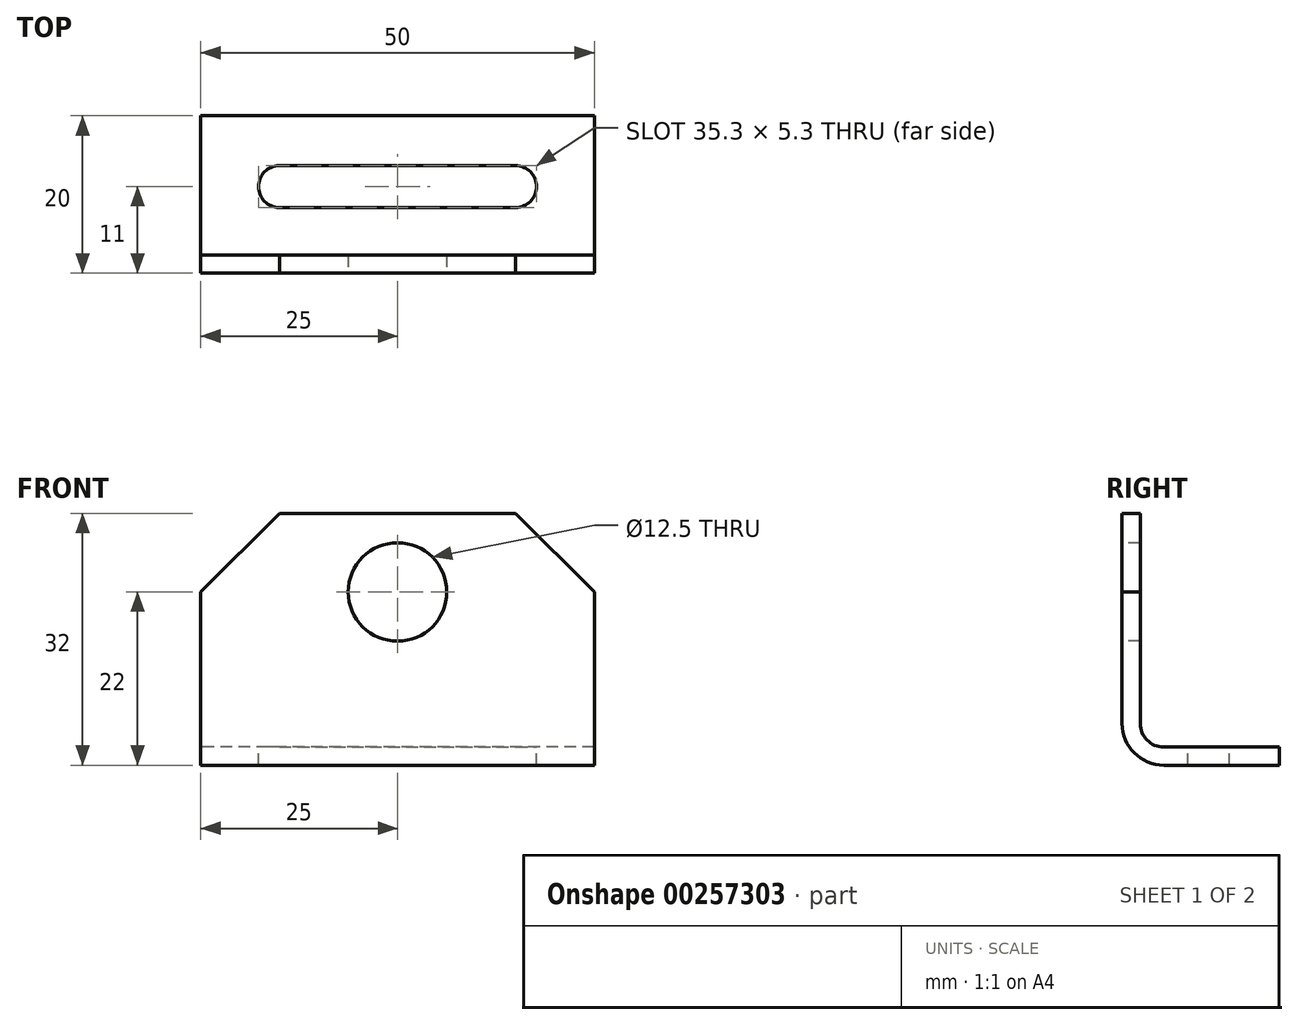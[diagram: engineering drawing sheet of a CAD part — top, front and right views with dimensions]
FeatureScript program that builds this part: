
annotation { "Feature Type Name" : "Feature", "Feature Type Description" : "" }
export const myFeature = defineFeature(function(context is Context, id is Id, definition is map)
    precondition{}
    {
        {
            var Q0;
            Q0=qCreatedBy(makeId("Right.planeOp"),FACE);
            var sketch = newSketch(context, id + "F0", { "sketchPlane" : qUnion([Q0])});
            skLineSegment(sketch, "E0", {"start": v(0, 32) * mm, "end": v(0, 0) * mm});
            skLineSegment(sketch, "E1", {"start": v(0, 0) * mm, "end": v(20, 0) * mm});
            skLineSegment(sketch, "E2", {"start": v(20, 0) * mm, "end": v(20, 2.3) * mm});
            skLineSegment(sketch, "E3", {"start": v(20, 2.3) * mm, "end": v(2.3, 2.3) * mm});
            skLineSegment(sketch, "E4", {"start": v(2.3, 2.3) * mm, "end": v(2.3, 32) * mm});
            skLineSegment(sketch, "E5", {"start": v(2.3, 32) * mm, "end": v(0, 32) * mm});
            skSolve(sketch);
        }
        {
            var Q0;
            Q0 = qSketchRegion(id + "F0", true);
            extrude(context, id + "F1", {"entities" : qUnion([Q0]), "depth" : 25 * mm, "hasSecondDirection" : true, "secondDirectionOppositeDirection" : true, "secondDirectionDepth" : 25 * mm});
        }
        {
            var Q0;
            Q0=makeQuery(id+"F1.opExtrude","SWEPT_FACE",FACE,{"disambiguationData":[OSD([sQuery(id+"F0.wireOp",EDGE,"E0")])]});
            var sketch = newSketch(context, id + "F2", { "sketchPlane" : qUnion([Q0])});
            skPoint(sketch, "E6", {"position": v(0, 22) * mm});
            skSolve(sketch);
        }
        {
            var Q0;
            Q0=makeQuery(id+"F1.opExtrude","SWEPT_FACE",FACE,{"disambiguationData":[OSD([sQuery(id+"F0.wireOp",EDGE,"E3")])]});
            var sketch = newSketch(context, id + "F3", { "sketchPlane" : qUnion([Q0])});
            skLineSegment(sketch, "E7", {"start": v(-20.02, 11) * mm, "end": v(21.78, 11) * mm, "construction": true});
            skLineSegment(sketch, "E8", {"start": v(15, 16.43) * mm, "end": v(15, 4.1) * mm, "construction": true});
            skArc(sketch, "E9", {"start": v(15, 8.35) * mm, "mid": v(17.65, 11) * mm, "end": v(15, 13.65) * mm});
            skLineSegment(sketch, "E10.0", {"start": v(-15.06, 8.35) * mm, "end": v(15, 8.35) * mm});
            skLineSegment(sketch, "E11.MirrorCS", {"start": v(-15.06, 13.65) * mm, "end": v(15, 13.65) * mm});
            skArc(sketch, "E12.MirrorC", {"start": v(-15, 8.35) * mm, "mid": v(-17.65, 11) * mm, "end": v(-15, 13.65) * mm});
            skPoint(sketch, "E13", {"position": v(-17.65, 11) * mm});
            skSolve(sketch);
        }
        {
            var Q0;
            {var subQ0=sQuery(id+"F3.wireOp",EDGE,"E9");Q0=makeQuery(id+"F3.imprint","IMPRINT",FACE,{"disambiguationData":[TD([[makeQuery(id+"F3.imprint","IMPRINT",EDGE,{"derivedFrom":subQ0}),1.0]])]});}
            extrude(context, id + "F4", {"entities" : qUnion([Q0]), "operationType" : NewBodyOperationType.REMOVE, "endBound" : BoundingType.THROUGH_ALL, "oppositeDirection" : true, "depth" : 25 * mm});
        }
        {
            var Q0;
            Q0=makeQuery(id+"F1.opExtrude","SWEPT_EDGE",EDGE,{"disambiguationData":[OSD([sQuery(id+"F0.wireOp",EDGE,"E3"),sQuery(id+"F0.wireOp",EDGE,"E4")])]});
            fillet(context, id + "F5", {"entities" : qUnion([Q0]), "radius" : 3 * mm, "tangentPropagation" : true, "allowEdgeOverflow" : false});
        }
        {
            var Q0;
            Q0=makeQuery(id+"F1.opExtrude","SWEPT_EDGE",EDGE,{"disambiguationData":[OSD([sQuery(id+"F0.wireOp",EDGE,"E0"),sQuery(id+"F0.wireOp",EDGE,"E1")])]});
            fillet(context, id + "F6", {"entities" : qUnion([Q0]), "radius" : 5.3 * mm, "tangentPropagation" : true, "allowEdgeOverflow" : false});
        }
        {
            var Q0;
            Q0=sQuery(id+"F2.wireOp",VERTEX,"E6");
            var Q1;
            Q1=makeQuery(id+"F1.opExtrude","SWEPT_BODY",BODY,{"disambiguationData":[OSD([sQuery(id+"F0.wireOp",EDGE,"E0"),sQuery(id+"F0.wireOp",EDGE,"E1"),sQuery(id+"F0.wireOp",EDGE,"E2"),sQuery(id+"F0.wireOp",EDGE,"E3"),sQuery(id+"F0.wireOp",EDGE,"E4"),sQuery(id+"F0.wireOp",EDGE,"E5")])]});
            hole(context, id + "F7", {"style" : HoleStyle.SIMPLE, "endStyle" : HoleEndStyle.THROUGH, "holeDiameter" : 12.5 * mm, "tappedDepth" : 12 * mm, "tapClearance" : 3, "locations" : qUnion([Q0]), "scope" : qUnion([Q1])});
        }
        {
            var Q0;
            Q0=makeQuery(id+"F1.opExtrude","CAP_EDGE",EDGE,{"disambiguationData":[OSD([sQuery(id+"F0.wireOp",EDGE,"E5")])],"isStart":false});
            var Q1;
            Q1=makeQuery(id+"F1.opExtrude","CAP_EDGE",EDGE,{"disambiguationData":[OSD([sQuery(id+"F0.wireOp",EDGE,"E5")])],"isStart":true});
            chamfer(context, id + "F8", {"entities" : qUnion([Q0, Q1]), "width" : 10 * mm, "tangentPropagation" : true});
        }
    });
